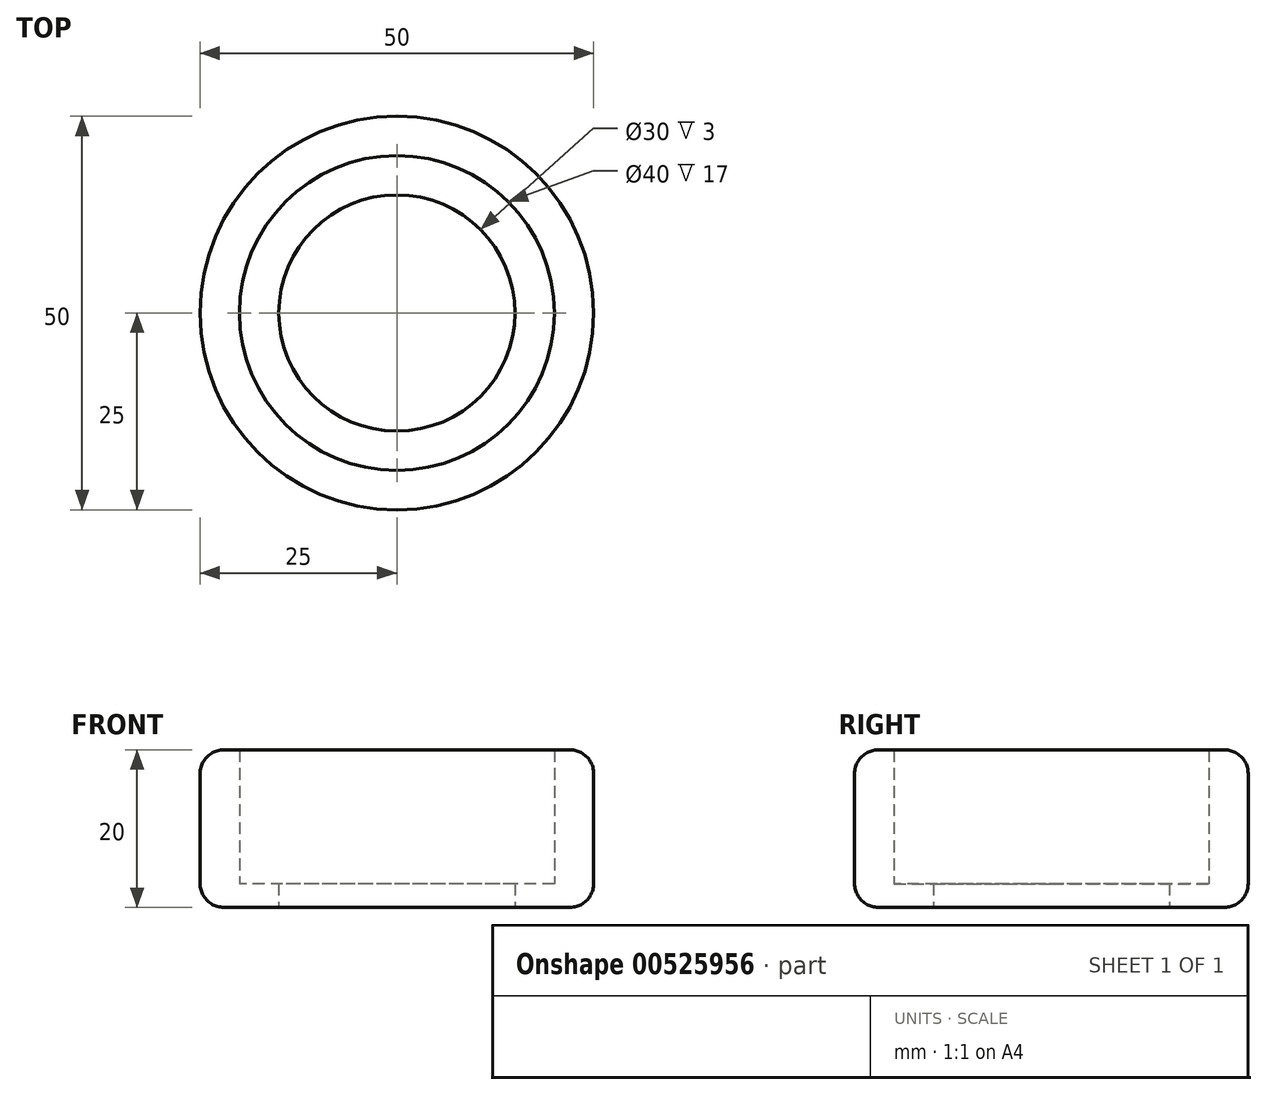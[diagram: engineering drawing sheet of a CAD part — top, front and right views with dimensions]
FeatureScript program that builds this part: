
annotation { "Feature Type Name" : "Feature", "Feature Type Description" : "" }
export const myFeature = defineFeature(function(context is Context, id is Id, definition is map)
    precondition{}
    {
        {
            var Q0;
            Q0=qCreatedBy(makeId("Top.planeOp"),FACE);
            var sketch = newSketch(context, id + "F0", { "sketchPlane" : qUnion([Q0])});
            skLineSegment(sketch, "E0.bottom", {"start": v(-25, 25) * mm, "end": v(25, 25) * mm});
            skLineSegment(sketch, "E0.top", {"start": v(-25, -25) * mm, "end": v(25, -25) * mm});
            skLineSegment(sketch, "E0.left", {"start": v(-25, 25) * mm, "end": v(-25, -25) * mm});
            skLineSegment(sketch, "E0.right", {"start": v(25, 25) * mm, "end": v(25, -25) * mm});
            skLineSegment(sketch, "E1", {"start": v(0, 25) * mm, "end": v(0, -25) * mm, "construction": true});
            skLineSegment(sketch, "E2", {"start": v(-25, 0) * mm, "end": v(25, 0) * mm, "construction": true});
            skCircle(sketch, "E3", {"center": v(0, 0) * mm, "radius": 15 * mm});
            skSolve(sketch);
        }
        {
            var Q0;
            Q0=makeQuery(id+"F0.imprint","IMPRINT",FACE,{"disambiguationData":[TD([[makeQuery(id+"F0.imprint","IMPRINT",EDGE,{"derivedFrom":sQuery(id+"F0.wireOp",EDGE,"E0.bottom")}),-1.0]])]});
            extrude(context, id + "F1", {"entities" : qUnion([Q0]), "depth" : 20 * mm, "offsetDistance" : 25 * mm});
        }
        {
            var Q0;
            Q0=qCreatedBy(makeId("Top.planeOp"),FACE);
            var sketch = newSketch(context, id + "F2", { "sketchPlane" : qUnion([Q0])});
            skCircle(sketch, "E4", {"center": v(0, 0) * mm, "radius": 20 * mm});
            skSolve(sketch);
        }
        {
            var Q0;
            Q0=qSketchRegion(id+"F2",true);
            extrude(context, id + "F3", {"entities" : qUnion([Q0]), "depth" : 20 * mm, "offsetDistance" : 25 * mm});
        }
        {
            var Q0;
            Q0=makeQuery(id+"F3.opExtrude","SWEPT_BODY",BODY,{"disambiguationData":[OSD([sQuery(id+"F2.wireOp",EDGE,"E4")])]});
            transform(context, id + "F4", {"entities" : qUnion([Q0]), "transformType" : TransformType.TRANSLATION_3D, "dx" : 0 * mm, "dy" : 0 * mm, "dz" : 3 * mm, "makeCopy" : false});
        }
        {
            var Q0;
            Q0=makeQuery(id+"F3.opExtrude","SWEPT_BODY",BODY,{"disambiguationData":[OSD([sQuery(id+"F2.wireOp",EDGE,"E4")])]});
            var Q1;
            Q1=makeQuery(id+"F1.opExtrude","SWEPT_BODY",BODY,{"disambiguationData":[OSD([sQuery(id+"F0.wireOp",EDGE,"E0.bottom"),sQuery(id+"F0.wireOp",EDGE,"E0.top"),sQuery(id+"F0.wireOp",EDGE,"E0.left"),sQuery(id+"F0.wireOp",EDGE,"E0.right"),sQuery(id+"F0.wireOp",EDGE,"E3")])]});
            booleanBodies(context, id + "F5", {"operationType" : BooleanOperationType.SUBTRACTION, "tools" : qUnion([Q0]), "targets" : qUnion([Q1])});
        }
        {
            var Q0;
            Q0=makeQuery(id+"F1.opExtrude","SWEPT_EDGE",EDGE,{"disambiguationData":[OSD([sQuery(id+"F0.wireOp",EDGE,"E0.bottom"),sQuery(id+"F0.wireOp",EDGE,"E0.left")])]});
            var Q1;
            Q1=makeQuery(id+"F1.opExtrude","SWEPT_EDGE",EDGE,{"disambiguationData":[OSD([sQuery(id+"F0.wireOp",EDGE,"E0.top"),sQuery(id+"F0.wireOp",EDGE,"E0.left")])]});
            var Q2;
            Q2=makeQuery(id+"F1.opExtrude","SWEPT_EDGE",EDGE,{"disambiguationData":[OSD([sQuery(id+"F0.wireOp",EDGE,"E0.top"),sQuery(id+"F0.wireOp",EDGE,"E0.right")])]});
            var Q3;
            Q3=makeQuery(id+"F1.opExtrude","SWEPT_EDGE",EDGE,{"disambiguationData":[OSD([sQuery(id+"F0.wireOp",EDGE,"E0.bottom"),sQuery(id+"F0.wireOp",EDGE,"E0.right")])]});
            fillet(context, id + "F6", {"entities" : qUnion([Q0, Q1, Q2, Q3]), "radius" : 25 * mm, "tangentPropagation" : true, "allowEdgeOverflow" : false});
        }
        {
            var Q0;
            {var subQ0=sQuery(id+"F0.wireOp",EDGE,"E0.left");var subQ1=sQuery(id+"F0.wireOp",EDGE,"E0.bottom");Q0=makeQuery(id+"F6.opFillet","BLEND_EDGE",EDGE,{"blendedFrom":[makeQuery(id+"F1.opExtrude","SWEPT_EDGE",EDGE,{"disambiguationData":[OSD([subQ1,subQ0])]}),makeQuery(id+"F1.opExtrude","CAP_FACE",FACE,{"disambiguationData":[OSD([subQ1,sQuery(id+"F0.wireOp",EDGE,"E0.top"),subQ0,sQuery(id+"F0.wireOp",EDGE,"E0.right"),sQuery(id+"F0.wireOp",EDGE,"E3")])],"isStart":true})],"blendedInto":[makeQuery(id+"F1.opExtrude","CAP_FACE",FACE,{"disambiguationData":[OSD([subQ1,sQuery(id+"F0.wireOp",EDGE,"E0.top"),subQ0,sQuery(id+"F0.wireOp",EDGE,"E0.right"),sQuery(id+"F0.wireOp",EDGE,"E3")])],"isStart":true})]});}
            var Q1;
            {var subQ0=sQuery(id+"F0.wireOp",EDGE,"E0.left");var subQ1=sQuery(id+"F0.wireOp",EDGE,"E0.bottom");Q1=makeQuery(id+"F6.opFillet","BLEND_EDGE",EDGE,{"blendedFrom":[makeQuery(id+"F1.opExtrude","SWEPT_EDGE",EDGE,{"disambiguationData":[OSD([subQ1,subQ0])]}),makeQuery(id+"F1.opExtrude","CAP_FACE",FACE,{"disambiguationData":[OSD([subQ1,sQuery(id+"F0.wireOp",EDGE,"E0.top"),subQ0,sQuery(id+"F0.wireOp",EDGE,"E0.right"),sQuery(id+"F0.wireOp",EDGE,"E3")])],"isStart":false})],"blendedInto":[makeQuery(id+"F1.opExtrude","CAP_FACE",FACE,{"disambiguationData":[OSD([subQ1,sQuery(id+"F0.wireOp",EDGE,"E0.top"),subQ0,sQuery(id+"F0.wireOp",EDGE,"E0.right"),sQuery(id+"F0.wireOp",EDGE,"E3")])],"isStart":false})]});}
            fillet(context, id + "F7", {"entities" : qUnion([Q0, Q1]), "radius" : 3 * mm, "tangentPropagation" : true, "allowEdgeOverflow" : false});
        }
    });
